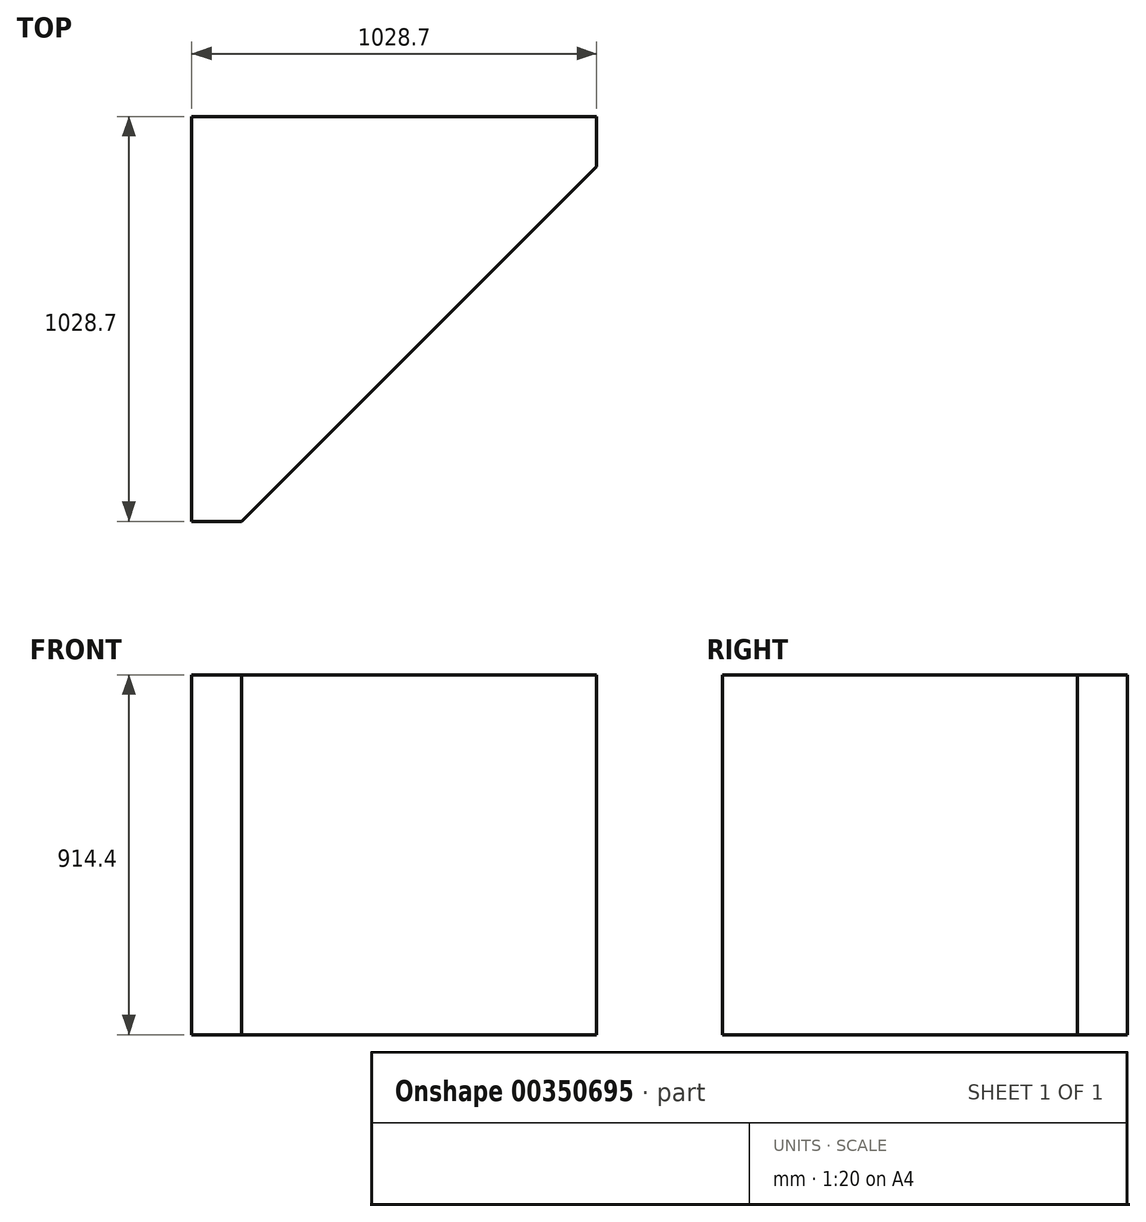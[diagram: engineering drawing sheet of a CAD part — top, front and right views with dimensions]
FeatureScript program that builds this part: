
annotation { "Feature Type Name" : "Feature", "Feature Type Description" : "" }
export const myFeature = defineFeature(function(context is Context, id is Id, definition is map)
    precondition{}
    {
        {
            var Q0;
            Q0=qCreatedBy(makeId("Top.planeOp"),FACE);
            var sketch = newSketch(context, id + "F0", { "sketchPlane" : qUnion([Q0])});
            skLineSegment(sketch, "E0", {"start": v(0, 0) * mm, "end": v(0, -1028.7) * mm});
            skLineSegment(sketch, "E1", {"start": v(0, -1028.7) * mm, "end": v(127, -1028.7) * mm});
            skLineSegment(sketch, "E2", {"start": v(127, -1028.7) * mm, "end": v(1028.7, -127) * mm});
            skLineSegment(sketch, "E3", {"start": v(1028.7, 0) * mm, "end": v(1028.7, -127) * mm});
            skLineSegment(sketch, "E4", {"start": v(1028.7, 0) * mm, "end": v(0, 0) * mm});
            skSolve(sketch);
        }
        {
            var Q0;
            Q0=makeQuery(id+"F0.imprint","IMPRINT",FACE,{"disambiguationData":[TD([[makeQuery(id+"F0.imprint","IMPRINT",EDGE,{"derivedFrom":sQuery(id+"F0.wireOp",EDGE,"E0")}),1.0]])]});
            extrude(context, id + "F1", {"entities" : qUnion([Q0]), "oppositeDirection" : true, "depth" : 914.4 * mm});
        }
    });
